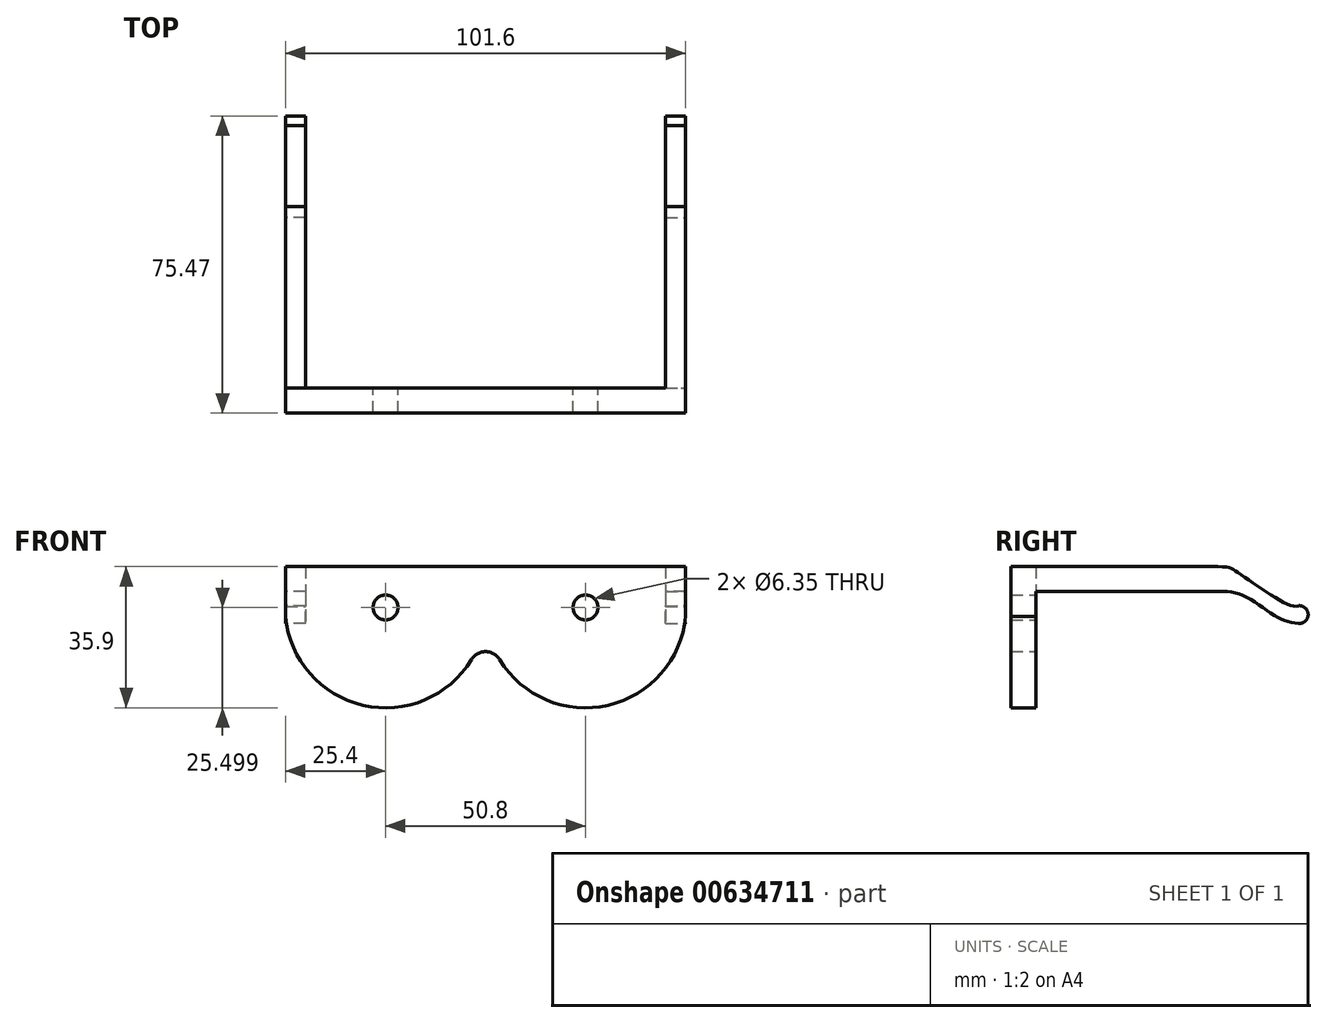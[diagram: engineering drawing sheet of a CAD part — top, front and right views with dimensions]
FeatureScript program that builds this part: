
annotation { "Feature Type Name" : "Feature", "Feature Type Description" : "" }
export const myFeature = defineFeature(function(context is Context, id is Id, definition is map)
    precondition{}
    {
        {
            var Q0;
            Q0=qCreatedBy(makeId("Front.planeOp"),FACE);
            var sketch = newSketch(context, id + "F0", { "sketchPlane" : qUnion([Q0])});
            skArc(sketch, "E0", {"start": v(-50.8, 0) * mm, "mid": v(-31.15, -22.55) * mm, "end": v(-3.6, -10.93) * mm});
            skLineSegment(sketch, "E1", {"start": v(0, 0) * mm, "end": v(0, 12.7) * mm});
            skLineSegment(sketch, "E2", {"start": v(0, 12.7) * mm, "end": v(-50.79, 12.7) * mm});
            skLineSegment(sketch, "E3", {"start": v(-50.79, 12.7) * mm, "end": v(-50.8, 0) * mm});
            skArc(sketch, "E4.MirrorCS", {"start": v(50.8, 0) * mm, "mid": v(31.15, -22.55) * mm, "end": v(3.6, -10.93) * mm});
            skLineSegment(sketch, "E5.MirrorCS", {"start": v(50.79, 12.7) * mm, "end": v(50.8, 0) * mm});
            skLineSegment(sketch, "E6.MirrorCS", {"start": v(0, 12.7) * mm, "end": v(50.79, 12.7) * mm});
            skArc(sketch, "E7", {"start": v(3.6, -10.93) * mm, "mid": v(0, -8.9) * mm, "end": v(-3.6, -10.93) * mm});
            skPoint(sketch, "E8.orphan", {"position": v(0, 0) * mm});
            skSolve(sketch);
        }
        {
            var Q0;
            Q0=makeQuery(id+"F0.imprint","IMPRINT",FACE,{"disambiguationData":[TD([[makeQuery(id+"F0.imprint","IMPRINT",EDGE,{"derivedFrom":sQuery(id+"F0.wireOp",EDGE,"E0")}),1.0]])]});
            extrude(context, id + "F1", {"entities" : qUnion([Q0]), "depth" : 6.35 * mm, "offsetDistance" : 25.4 * mm});
        }
        {
            var Q0;
            Q0=makeQuery(id+"F1.opExtrude","SWEPT_FACE",FACE,{"disambiguationData":[OSD([sQuery(id+"F0.wireOp",EDGE,"E5.MirrorCS")])]});
            var sketch = newSketch(context, id + "F2", { "sketchPlane" : qUnion([Q0])});
            skLineSegment(sketch, "E9", {"start": v(-6.35, 12.66) * mm, "end": v(46.13, 12.66) * mm});
            skLineSegment(sketch, "E10", {"start": v(-6.35, 12.66) * mm, "end": v(-6.35, 6.3) * mm});
            skLineSegment(sketch, "E11", {"start": v(-6.35, 6.3) * mm, "end": v(43.37, 6.3) * mm});
            skFitSpline(sketch, "E12", {"points": [v(43.37, 6.3) * mm, v(52.7, 5.25) * mm, v(60.92, 0) * mm, v(66.65, -1.78) * mm], "startDerivative": vector(37.5, 0.8) * mm, "endDerivative": vector(23, -2.2) * mm});
            skFitSpline(sketch, "E13", {"points": [v(46.13, 12.66) * mm, v(50.7, 11.53) * mm, v(60.57, 4.88) * mm, v(66.65, 2.7) * mm], "startDerivative": vector(33.02, -0.77) * mm, "endDerivative": vector(13, 5.78) * mm});
            skArc(sketch, "E14", {"start": v(66.65, -1.78) * mm, "mid": v(69.12, 0.46) * mm, "end": v(66.65, 2.7) * mm});
            skSolve(sketch);
        }
        {
            var Q0;
            {var subQ1=sQuery(id+"F2.wireOp",EDGE,"E12");Q0=makeQuery(id+"F2.imprint","IMPRINT",FACE,{"disambiguationData":[TD([[makeQuery(id+"F2.imprint","IMPRINT",EDGE,{"derivedFrom":subQ1}),1.0]])]});}
            extrude(context, id + "F3", {"entities" : qUnion([Q0]), "oppositeDirection" : true, "depth" : 5.08 * mm, "offsetDistance" : 25.4 * mm});
        }
        {
            var Q0;
            Q0=makeQuery(id+"F3.opExtrude","SWEPT_BODY",BODY,{"disambiguationData":[OSD([sQuery(id+"F0.wireOp",EDGE,"E5.MirrorCS"),sQuery(id+"F2.wireOp",EDGE,"E9"),sQuery(id+"F2.wireOp",EDGE,"E11"),sQuery(id+"F2.wireOp",EDGE,"E12"),sQuery(id+"F2.wireOp",EDGE,"E13"),sQuery(id+"F2.wireOp",EDGE,"E14")])]});
            var Q1;
            Q1=qCreatedBy(makeId("Right.planeOp"),FACE);
            mirror(context, id + "F4", {"operationType" : NewBodyOperationType.ADD, "entities" : qUnion([Q0]), "mirrorPlane" : qUnion([Q1])});
        }
        {
            var Q0;
            Q0=qCreatedBy(makeId("Front.planeOp"),FACE);
            var sketch = newSketch(context, id + "F5", { "sketchPlane" : qUnion([Q0])});
            skLineSegment(sketch, "E15.0", {"start": v(-47.24, 9.14) * mm, "end": v(-47.24, 0.17) * mm});
            skLineSegment(sketch, "E15.1", {"start": v(47.24, 9.14) * mm, "end": v(47.24, 0.17) * mm});
            skArc(sketch, "E15.2", {"start": v(47.24, 0.17) * mm, "mid": v(30.27, -19.1) * mm, "end": v(6.63, -9.08) * mm});
            skLineSegment(sketch, "E15.3", {"start": v(-47.24, 9.14) * mm, "end": v(47.24, 9.14) * mm});
            skArc(sketch, "E15.4", {"start": v(6.63, -9.08) * mm, "mid": v(0, -5.35) * mm, "end": v(-6.63, -9.08) * mm});
            skArc(sketch, "E15.5", {"start": v(-47.24, 0.17) * mm, "mid": v(-30.27, -19.1) * mm, "end": v(-6.63, -9.08) * mm});
            skSolve(sketch);
        }
        {
            var Q0;
            Q0=sQuery(id+"F5.wireOp",VERTEX,"E15.2.center");
            var Q1;
            Q1=sQuery(id+"F5.wireOp",VERTEX,"E15.5.center");
            var Q2;
            Q2=makeQuery(id+"F1.opExtrude","SWEPT_BODY",BODY,{"disambiguationData":[OSD([sQuery(id+"F0.wireOp",EDGE,"E0"),sQuery(id+"F0.wireOp",EDGE,"E2"),sQuery(id+"F0.wireOp",EDGE,"E3"),sQuery(id+"F0.wireOp",EDGE,"E4.MirrorCS"),sQuery(id+"F0.wireOp",EDGE,"E5.MirrorCS"),sQuery(id+"F0.wireOp",EDGE,"E6.MirrorCS"),sQuery(id+"F0.wireOp",EDGE,"E7")])]});
            hole(context, id + "F6", {"style" : HoleStyle.SIMPLE, "endStyle" : HoleEndStyle.THROUGH, "oppositeDirection" : true, "holeDiameter" : 6.35 * mm, "majorDiameter" : 6.35 * mm, "isTappedThrough" : true, "tappedDepth" : 12.7 * mm, "tapClearance" : 3, "locations" : qUnion([Q0, Q1]), "scope" : qUnion([Q2])});
        }
    });
